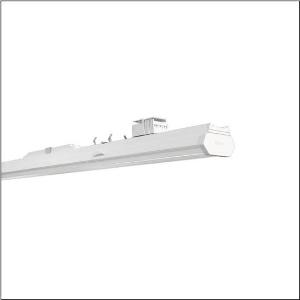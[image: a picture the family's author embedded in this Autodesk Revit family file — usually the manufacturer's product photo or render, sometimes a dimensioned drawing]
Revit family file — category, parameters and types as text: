
# Revit family: licross_r__21_protected_mo_52td1bvn48xg_aeae
name_source: partatom
category: Lighting Fixtures
units: mm (PartAtom-declared; Revit-internal decimal feet)

## family parameters
Cut with Voids When Loaded = No
Host = Face
Light Source = No
Part Type = Normal
Room Calculation Point = No
Round Connector Dimension = Use Diameter
Shared = No

## types (1)
- --- (1 x LED, 8000 lm, 48.3 W, 4000K)
    Apparent Load = 48 VA
    CIE Flux Codes = 54 82 95 97 100
    Color Rendering = 80
    Color Temperature = 4000K
    Default Elevation = 1800 mm
    Description = Licross® 21 Protected MO, luminaire insert, of sheet steel, galvanised, coil coated, white, length: 1.500mm, width: 90mm, height: 101mm, LED rated luminous flux: 8.000lm, light colour: 840, SDCM (Standard Deviation of Colour Matching)MacAdam ≤ 3 SDCM (initial), control gear: DALI 2, CLO, with plug, 5-pole, with phase selection, mains connection: 220..240V, AC, 50/60Hz, start of lifetime: 48W, end of service life: 58W, internal wiring halogen-free, primary optical cover: cover, of PMMA, light emission: direct distribution, primary light characteristic: symmetric, protection rating (complete): IP54, insulation class (complete): insulation class I (protective earthing), certification: CE, ENEC, VDE, UKCA, protection symbol: D if used in an environment with non-conductive dust loads with corresponding accessories, impact resistance: IK06, permissible ambient temperature for indoor applications: -25..+40°C, corresponds to IFS (International Featured Standards) requirements for safety and quality in the food industry, reducing of maximum allowable ambient temperature of 5°C with ceiling mounting, LABS conformity tested according to VDMA 24364:2018-05, packaging unit: 1 piece
    Height = 92 mm
    Lamp = 1 x LED
    Lamp Light Flux = 8000 lm
    Lamp Power = 48.3 W
    Lamp count = 1
    Length = 1500 mm
    Luminous efficacy = 166 lm/W
    Manufacturer = Siteco
    ModVariant = No
    Model = 52TD1BVN48XG
    Mounting Place = Ceiling
    Mounting Type = Pendant
    Number of Poles = 1
    OnlyDefault = Yes
    Power Factor = 1
    Product Name = Licross® 21 Protected MO
    Product group = luminaire insert | ceiling pendant
    ProductGroupID = 901
    Protection Class = Protection class I
    Protection Degree = IP 54
    RLX_Detail_Level = 1
    RLX_Emergency_Light_Flux = 0 lm
    RLX_Emergency_Type = 0
    RLX_Emergency_Type_DB = No
    RlxData = <blob elided: 24517 chars, md5=5658d267>
    Socket = socket
    Standby Power = 0 W
    System Light Flux = 8000 lm
    System Power = 48 W
    Type Comments = factory setting: luminous flux: 100 % | dim-lin: 254 | 326 mA
    Type Image = l_1256148.jpg
    URL = http://relux.com
    VarID = @adj_090587
    Voltage = 0 V
    Weight = 0.00 kg
    Width = 88 mm

## geometry (parser evidence)
native form markers: Blend x4, Sweep x10
no freeform markers — native parametric forms only
